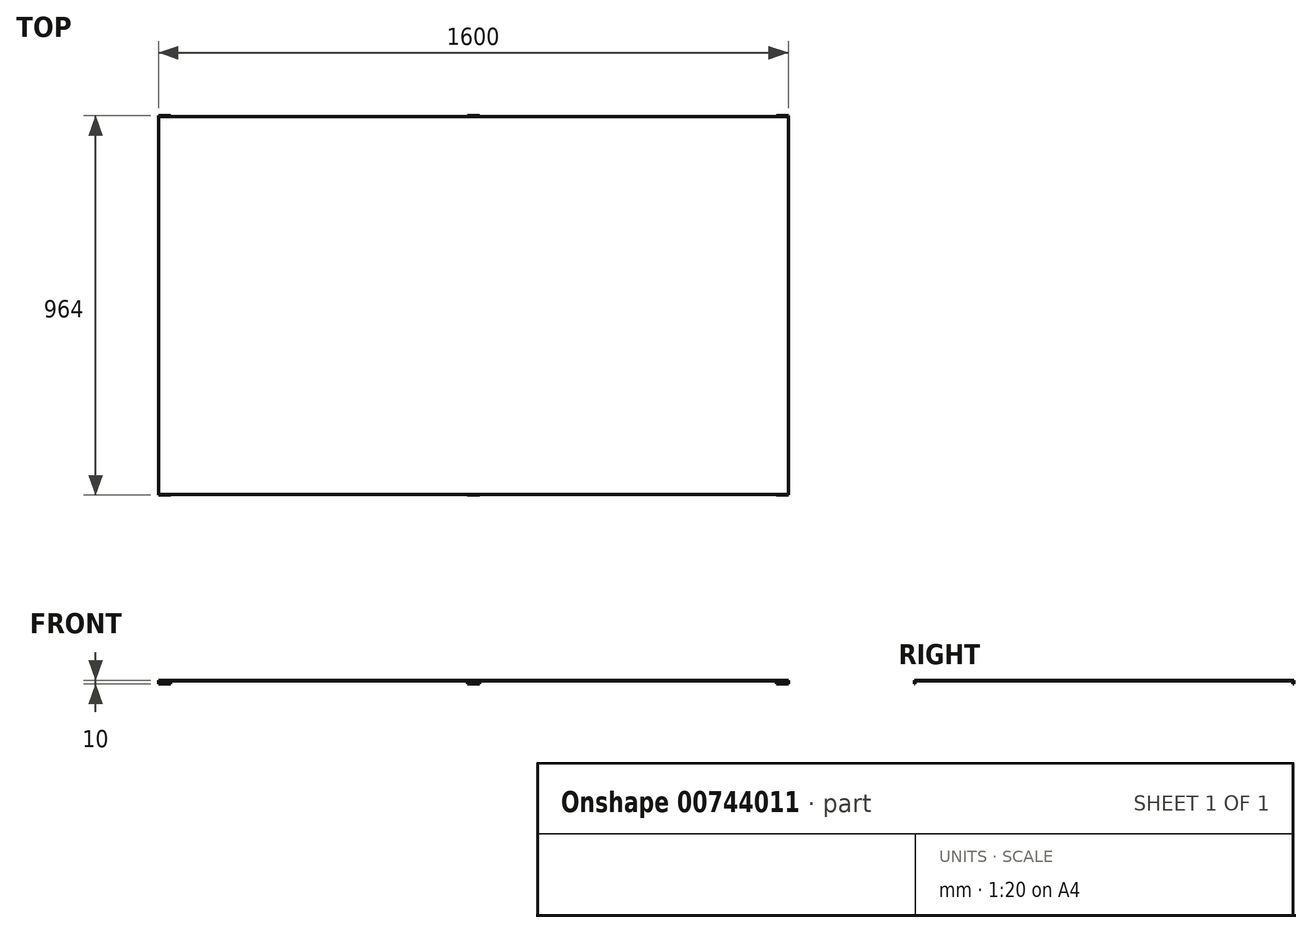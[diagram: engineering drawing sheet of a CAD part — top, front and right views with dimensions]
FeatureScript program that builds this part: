
annotation { "Feature Type Name" : "Feature", "Feature Type Description" : "" }
export const myFeature = defineFeature(function(context is Context, id is Id, definition is map)
    precondition{}
    {
        {
            var Q0;
            Q0=qCreatedBy(makeId("Top.planeOp"),FACE);
            var sketch = newSketch(context, id + "F0", { "sketchPlane" : qUnion([Q0])});
            skLineSegment(sketch, "E0.bottom", {"start": v(-800, 480) * mm, "end": v(800, 480) * mm});
            skLineSegment(sketch, "E0.top", {"start": v(-800, -480) * mm, "end": v(800, -480) * mm});
            skLineSegment(sketch, "E0.left", {"start": v(-800, 480) * mm, "end": v(-800, -480) * mm});
            skLineSegment(sketch, "E0.right", {"start": v(800, 480) * mm, "end": v(800, -480) * mm});
            skPoint(sketch, "E0.middle", {"position": v(0, 0) * mm});
            skSolve(sketch);
        }
        {
            var Q0;
            Q0 = qSketchRegion(id + "F0", true);
            extrude(context, id + "F1", {"entities" : qUnion([Q0]), "oppositeDirection" : true, "depth" : 2 * mm, "offsetDistance" : 25 * mm});
        }
        {
            var Q0;
            Q0=makeQuery(id+"F1.opExtrude","CAP_FACE",FACE,{"disambiguationData":[OSD([sQuery(id+"F0.wireOp",EDGE,"E0.bottom"),sQuery(id+"F0.wireOp",EDGE,"E0.top"),sQuery(id+"F0.wireOp",EDGE,"E0.left"),sQuery(id+"F0.wireOp",EDGE,"E0.right")])],"isStart":true});
            var sketch = newSketch(context, id + "F2", { "sketchPlane" : qUnion([Q0])});
            skLineSegment(sketch, "E1.bottom", {"start": v(-15, 482) * mm, "end": v(15, 482) * mm});
            skLineSegment(sketch, "E1.top", {"start": v(-15, 480) * mm, "end": v(15, 480) * mm});
            skLineSegment(sketch, "E1.left", {"start": v(-15, 482) * mm, "end": v(-15, 480) * mm});
            skLineSegment(sketch, "E1.right", {"start": v(15, 482) * mm, "end": v(15, 480) * mm});
            skLineSegment(sketch, "E2", {"start": v(0, -480) * mm, "end": v(0, 480) * mm, "construction": true});
            skLineSegment(sketch, "E3", {"start": v(0, 480) * mm, "end": v(0, 482) * mm, "construction": true});
            skLineSegment(sketch, "E4.bottom", {"start": v(770, 482) * mm, "end": v(800, 482) * mm});
            skLineSegment(sketch, "E4.top", {"start": v(770, 480) * mm, "end": v(800, 480) * mm});
            skLineSegment(sketch, "E4.left", {"start": v(770, 482) * mm, "end": v(770, 480) * mm});
            skLineSegment(sketch, "E4.right", {"start": v(800, 482) * mm, "end": v(800, 480) * mm});
            skLineSegment(sketch, "E5", {"start": v(785, 480) * mm, "end": v(785, 482) * mm, "construction": true});
            skLineSegment(sketch, "E6.bottom", {"start": v(-800, 482) * mm, "end": v(-770, 482) * mm});
            skLineSegment(sketch, "E6.top", {"start": v(-800, 480) * mm, "end": v(-770, 480) * mm});
            skLineSegment(sketch, "E6.left", {"start": v(-800, 482) * mm, "end": v(-800, 480) * mm});
            skLineSegment(sketch, "E6.right", {"start": v(-770, 482) * mm, "end": v(-770, 480) * mm});
            skLineSegment(sketch, "E7", {"start": v(-785, 480) * mm, "end": v(-785, 482) * mm, "construction": true});
            skLineSegment(sketch, "E8.bottom", {"start": v(-15, -480) * mm, "end": v(15, -480) * mm});
            skLineSegment(sketch, "E8.top", {"start": v(-15, -482) * mm, "end": v(15, -482) * mm});
            skLineSegment(sketch, "E8.left", {"start": v(-15, -480) * mm, "end": v(-15, -482) * mm});
            skLineSegment(sketch, "E8.right", {"start": v(15, -480) * mm, "end": v(15, -482) * mm});
            skLineSegment(sketch, "E9", {"start": v(0, -482) * mm, "end": v(0, -480) * mm, "construction": true});
            skLineSegment(sketch, "E10.bottom", {"start": v(770, -480) * mm, "end": v(800, -480) * mm});
            skLineSegment(sketch, "E10.top", {"start": v(770, -482) * mm, "end": v(800, -482) * mm});
            skLineSegment(sketch, "E10.left", {"start": v(770, -480) * mm, "end": v(770, -482) * mm});
            skLineSegment(sketch, "E10.right", {"start": v(800, -480) * mm, "end": v(800, -482) * mm});
            skLineSegment(sketch, "E11", {"start": v(785, -482) * mm, "end": v(785, -480) * mm, "construction": true});
            skLineSegment(sketch, "E12.bottom", {"start": v(-800, -480) * mm, "end": v(-770, -480) * mm});
            skLineSegment(sketch, "E12.top", {"start": v(-800, -482) * mm, "end": v(-770, -482) * mm});
            skLineSegment(sketch, "E12.left", {"start": v(-800, -480) * mm, "end": v(-800, -482) * mm});
            skLineSegment(sketch, "E12.right", {"start": v(-770, -480) * mm, "end": v(-770, -482) * mm});
            skLineSegment(sketch, "E13", {"start": v(-785, -482) * mm, "end": v(-785, -480) * mm, "construction": true});
            skSolve(sketch);
        }
        {
            var Q0;
            Q0 = qSketchRegion(id + "F2", true);
            extrude(context, id + "F3", {"entities" : qUnion([Q0]), "oppositeDirection" : true, "depth" : 10 * mm, "offsetDistance" : 25 * mm});
        }
    });
